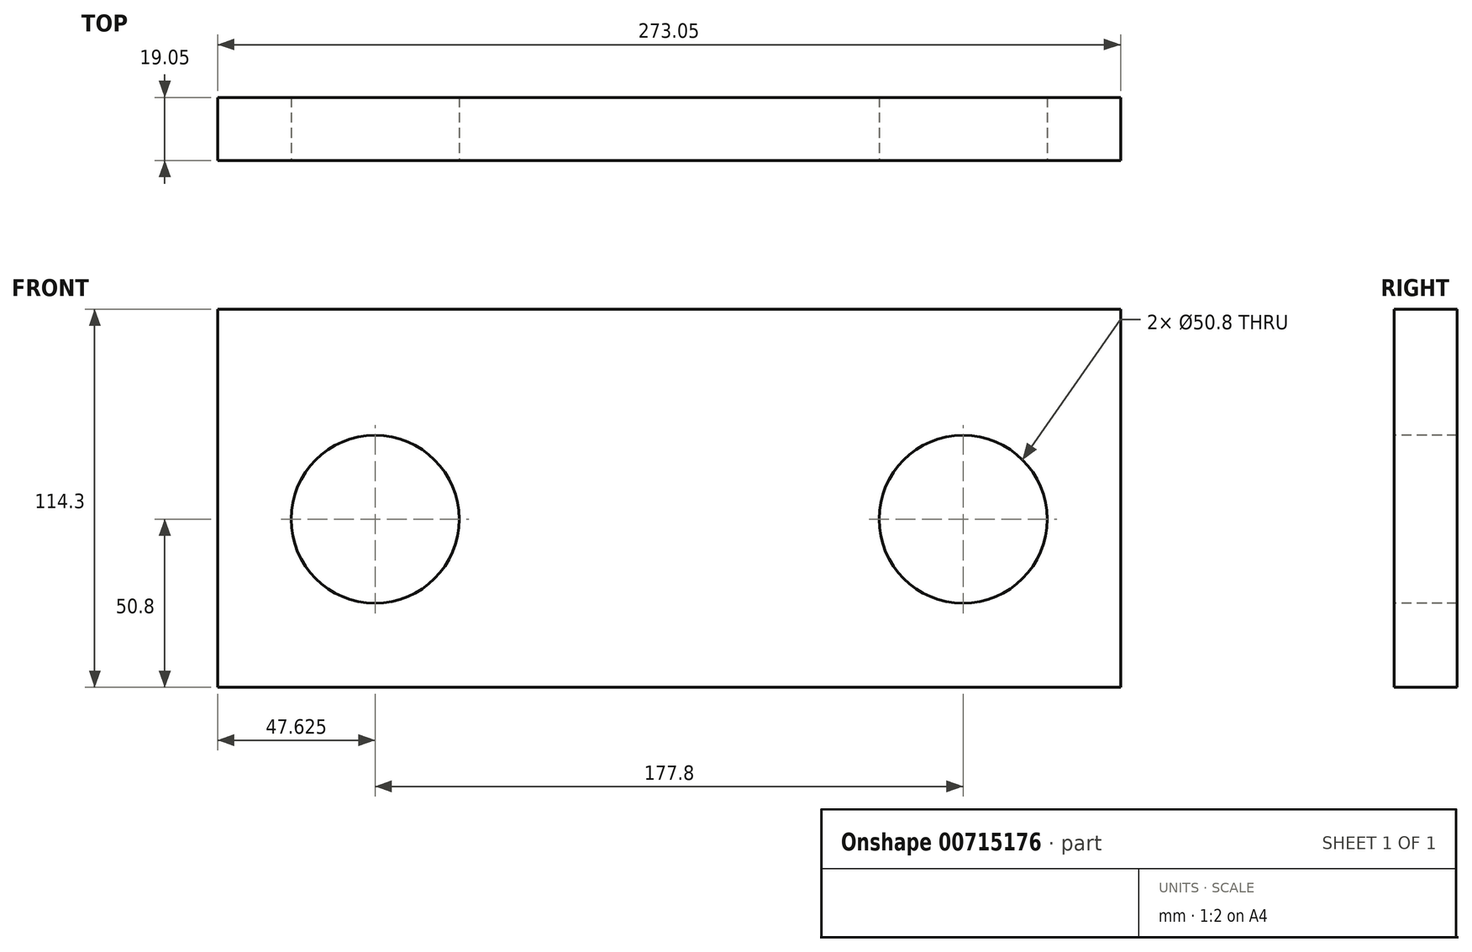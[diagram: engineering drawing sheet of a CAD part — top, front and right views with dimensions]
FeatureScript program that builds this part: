
annotation { "Feature Type Name" : "Feature", "Feature Type Description" : "" }
export const myFeature = defineFeature(function(context is Context, id is Id, definition is map)
    precondition{}
    {
        {
            var Q0;
            Q0=qCreatedBy(makeId("Front.planeOp"),FACE);
            var sketch = newSketch(context, id + "F0", { "sketchPlane" : qUnion([Q0])});
            skLineSegment(sketch, "E0.bottom", {"start": v(0, 0) * mm, "end": v(273.05, 0) * mm});
            skLineSegment(sketch, "E0.top", {"start": v(0, 114.3) * mm, "end": v(273.05, 114.3) * mm});
            skLineSegment(sketch, "E0.left", {"start": v(0, 0) * mm, "end": v(0, 114.3) * mm});
            skLineSegment(sketch, "E0.right", {"start": v(273.05, 0) * mm, "end": v(273.05, 114.3) * mm});
            skSolve(sketch);
        }
        {
            var Q0;
            Q0=qSketchRegion(id+"F0",true);
            extrude(context, id + "F1", {"entities" : qUnion([Q0]), "depth" : 19.05 * mm, "offsetDistance" : 25.4 * mm});
        }
        {
            var Q0;
            Q0=makeQuery(id+"F1.opExtrude","CAP_FACE",FACE,{"disambiguationData":[OSD([sQuery(id+"F0.wireOp",EDGE,"E0.bottom"),sQuery(id+"F0.wireOp",EDGE,"E0.top"),sQuery(id+"F0.wireOp",EDGE,"E0.left"),sQuery(id+"F0.wireOp",EDGE,"E0.right")])],"isStart":false});
            var sketch = newSketch(context, id + "F2", { "sketchPlane" : qUnion([Q0])});
            skCircle(sketch, "E1", {"center": v(47.63, 50.8) * mm, "radius": 25.4 * mm});
            skCircle(sketch, "E2", {"center": v(225.43, 50.8) * mm, "radius": 25.4 * mm});
            skSolve(sketch);
        }
        {
            var Q0;
            Q0 = qSketchRegion(id + "F2", true);
            extrude(context, id + "F3", {"entities" : qUnion([Q0]), "operationType" : NewBodyOperationType.REMOVE, "oppositeDirection" : true, "depth" : 25.4 * mm, "offsetDistance" : 25.4 * mm});
        }
    });
